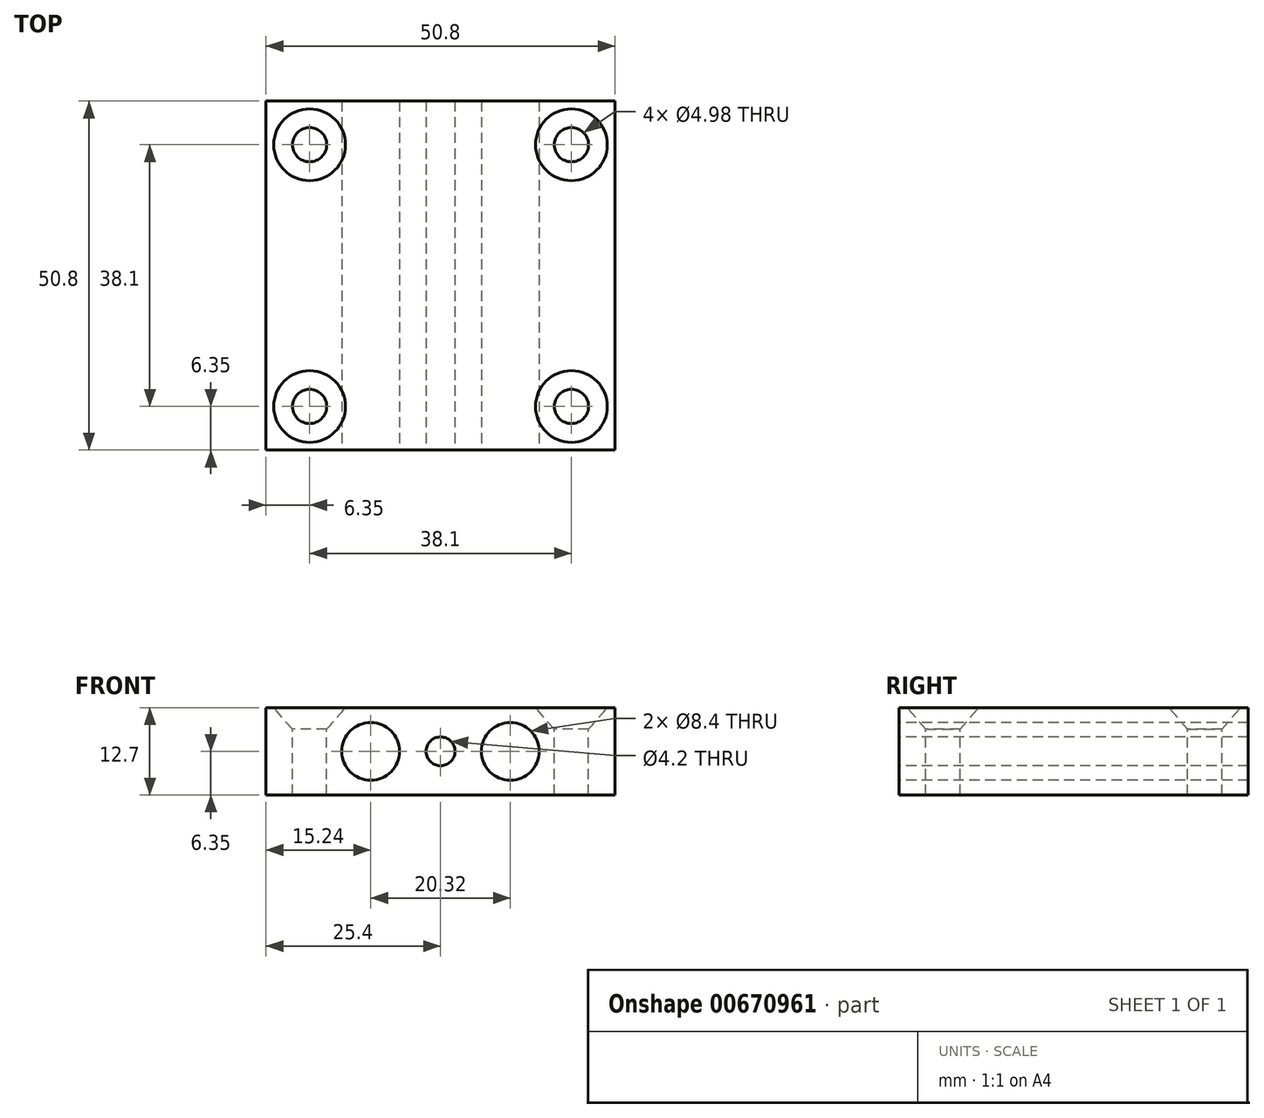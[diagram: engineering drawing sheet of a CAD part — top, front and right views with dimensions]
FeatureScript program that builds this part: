
annotation { "Feature Type Name" : "Feature", "Feature Type Description" : "" }
export const myFeature = defineFeature(function(context is Context, id is Id, definition is map)
    precondition{}
    {
        {
            var Q0;
            Q0=qCreatedBy(makeId("Top.planeOp"),FACE);
            var sketch = newSketch(context, id + "F0", { "sketchPlane" : qUnion([Q0])});
            skLineSegment(sketch, "E0.bottom", {"start": v(50.8, 50.8) * mm, "end": v(0, 50.8) * mm});
            skLineSegment(sketch, "E0.top", {"start": v(50.8, 0) * mm, "end": v(0, 0) * mm});
            skLineSegment(sketch, "E0.left", {"start": v(50.8, 50.8) * mm, "end": v(50.8, 0) * mm});
            skLineSegment(sketch, "E0.right", {"start": v(0, 50.8) * mm, "end": v(0, 0) * mm});
            skSolve(sketch);
        }
        {
            var Q0;
            Q0=makeQuery(id+"F0.imprint","IMPRINT",FACE,{"disambiguationData":[TD([[makeQuery(id+"F0.imprint","IMPRINT",EDGE,{"derivedFrom":sQuery(id+"F0.wireOp",EDGE,"E0.bottom")}),1.0]])]});
            extrude(context, id + "F1", {"entities" : qUnion([Q0]), "oppositeDirection" : true, "depth" : 6.35 * mm, "offsetDistance" : 25.4 * mm, "hasSecondDirection" : true, "secondDirectionOppositeDirection" : false, "secondDirectionDepth" : 6.35 * mm});
        }
        {
            var Q0;
            Q0=makeQuery(id+"F1.opExtrude","SWEPT_FACE",FACE,{"disambiguationData":[OSD([sQuery(id+"F0.wireOp",EDGE,"E0.top")])]});
            var sketch = newSketch(context, id + "F2", { "sketchPlane" : qUnion([Q0])});
            skPoint(sketch, "E1", {"position": v(25.4, 0) * mm});
            skPoint(sketch, "E2", {"position": v(15.24, 0) * mm});
            skPoint(sketch, "E3", {"position": v(35.56, 0) * mm});
            skLineSegment(sketch, "E4", {"start": v(25.4, 0) * mm, "end": v(35.56, 0) * mm, "construction": true});
            skLineSegment(sketch, "E5", {"start": v(25.4, 0) * mm, "end": v(15.24, 0) * mm, "construction": true});
            skPoint(sketch, "E6", {"position": v(25.4, 6.35) * mm});
            skPoint(sketch, "E7", {"position": v(44.27, 56.55) * mm});
            skSolve(sketch);
        }
        {
            var Q0;
            Q0=sQuery(id+"F2.wireOp",VERTEX,"E2");
            var Q1;
            Q1=sQuery(id+"F2.wireOp",VERTEX,"E3");
            var Q2;
            Q2=makeQuery(id+"F1.opExtrude","SWEPT_BODY",BODY,{"disambiguationData":[OSD([sQuery(id+"F0.wireOp",EDGE,"E0.bottom"),sQuery(id+"F0.wireOp",EDGE,"E0.top"),sQuery(id+"F0.wireOp",EDGE,"E0.left"),sQuery(id+"F0.wireOp",EDGE,"E0.right")])]});
            hole(context, id + "F3", {"style" : HoleStyle.SIMPLE, "endStyle" : HoleEndStyle.THROUGH, "standardTappedOrClearance" : lookupTablePath({ "standard" : "ISO", "fit" : "Close", "size" : "M8", "type" : "Clearance" }), "standardBlindInLast" : lookupTablePath({ "fit" : "Close", "standard" : "ISO", "size" : "M8", "type" : "Clearance" }), "holeDiameter" : 8.4 * mm, "majorDiameter" : 6.35 * mm, "isTappedThrough" : true, "tappedDepth" : 12.7 * mm, "tapClearance" : 3, "locations" : qUnion([Q0, Q1]), "scope" : qUnion([Q2])});
        }
        {
            var Q0;
            Q0=makeQuery(id+"F1.opExtrude","CAP_FACE",FACE,{"disambiguationData":[OSD([sQuery(id+"F0.wireOp",EDGE,"E0.bottom"),sQuery(id+"F0.wireOp",EDGE,"E0.top"),sQuery(id+"F0.wireOp",EDGE,"E0.left"),sQuery(id+"F0.wireOp",EDGE,"E0.right")])],"isStart":true});
            var sketch = newSketch(context, id + "F4", { "sketchPlane" : qUnion([Q0])});
            skLineSegment(sketch, "E8", {"start": v(6.35, 0) * mm, "end": v(6.35, 6.35) * mm, "construction": true});
            skLineSegment(sketch, "E9", {"start": v(6.35, 6.35) * mm, "end": v(0, 6.35) * mm, "construction": true});
            skLineSegment(sketch, "E10", {"start": v(0, 44.45) * mm, "end": v(6.35, 44.45) * mm, "construction": true});
            skLineSegment(sketch, "E11", {"start": v(6.35, 44.45) * mm, "end": v(6.35, 50.8) * mm, "construction": true});
            skLineSegment(sketch, "E12", {"start": v(44.45, 50.8) * mm, "end": v(44.45, 44.45) * mm, "construction": true});
            skLineSegment(sketch, "E13", {"start": v(44.45, 44.45) * mm, "end": v(50.8, 44.45) * mm, "construction": true});
            skLineSegment(sketch, "E14", {"start": v(50.8, 6.35) * mm, "end": v(44.45, 6.35) * mm, "construction": true});
            skLineSegment(sketch, "E15", {"start": v(44.45, 6.35) * mm, "end": v(44.45, 0) * mm, "construction": true});
            skSolve(sketch);
        }
        {
            var Q0;
            Q0=sQuery(id+"F4.wireOp",VERTEX,"E10.end");
            var Q1;
            Q1=sQuery(id+"F4.wireOp",VERTEX,"E9.start");
            var Q2;
            Q2=sQuery(id+"F4.wireOp",VERTEX,"E15.start");
            var Q3;
            Q3=sQuery(id+"F4.wireOp",VERTEX,"E13.start");
            var Q4;
            Q4=makeQuery(id+"F1.opExtrude","SWEPT_BODY",BODY,{"disambiguationData":[OSD([sQuery(id+"F0.wireOp",EDGE,"E0.bottom"),sQuery(id+"F0.wireOp",EDGE,"E0.top"),sQuery(id+"F0.wireOp",EDGE,"E0.left"),sQuery(id+"F0.wireOp",EDGE,"E0.right")])]});
            hole(context, id + "F5", {"style" : HoleStyle.C_SINK, "endStyle" : HoleEndStyle.THROUGH, "standardTappedOrClearance" : lookupTablePath({ "fit" : "Close", "standard" : "ANSI", "size" : "#10", "type" : "Clearance" }), "standardBlindInLast" : lookupTablePath({ "fit" : "Close", "standard" : "ANSI", "size" : "#10", "type" : "Clearance" }), "holeDiameter" : 4.98 * mm, "cSinkDiameter" : 10.44 * mm, "cSinkAngle" : 82 * degree, "majorDiameter" : 6.35 * mm, "isTappedThrough" : true, "tappedDepth" : 12.7 * mm, "tapClearance" : 3, "locations" : qUnion([Q0, Q1, Q2, Q3]), "scope" : qUnion([Q4])});
        }
        {
            var Q0;
            Q0=sQuery(id+"F2.wireOp",VERTEX,"E4.start");
            var Q1;
            Q1=makeQuery(id+"F1.opExtrude","SWEPT_BODY",BODY,{"disambiguationData":[OSD([sQuery(id+"F0.wireOp",EDGE,"E0.bottom"),sQuery(id+"F0.wireOp",EDGE,"E0.top"),sQuery(id+"F0.wireOp",EDGE,"E0.left"),sQuery(id+"F0.wireOp",EDGE,"E0.right")])]});
            hole(context, id + "F6", {"style" : HoleStyle.SIMPLE, "endStyle" : HoleEndStyle.THROUGH, "standardTappedOrClearance" : lookupTablePath({ "standard" : "ISO", "engagement" : "75%", "pitch" : "0.8 mm", "size" : "M5", "type" : "Tapped" }), "standardBlindInLast" : lookupTablePath({ "standard" : "ISO", "engagement" : "75%", "pitch" : "0.8 mm", "size" : "M5", "type" : "Tapped" }), "holeDiameter" : 4.2 * mm, "majorDiameter" : 5 * mm, "showTappedDepth" : true, "isTappedThrough" : true, "tappedDepth" : 12.7 * mm, "tapClearance" : 3, "locations" : qUnion([Q0]), "scope" : qUnion([Q1])});
        }
    });
